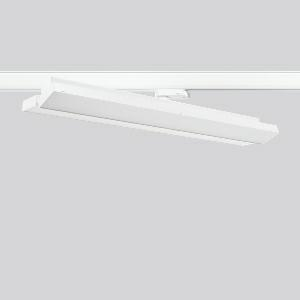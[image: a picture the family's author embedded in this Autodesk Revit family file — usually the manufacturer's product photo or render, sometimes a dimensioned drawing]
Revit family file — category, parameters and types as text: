
# Revit family: tx-move_742164_002_3_6d08
name_source: partatom
category: Lighting Fixtures
units: mm (PartAtom-declared; Revit-internal decimal feet)

## family parameters
Cut with Voids When Loaded = No
Host = Face
Light Source = No
Part Type = Normal
Room Calculation Point = No
Round Connector Dimension = Use Diameter
Shared = No

## types (1)
- MultiLumen 1 (1 x LED Modul 835, 2550 lm, 3500)
    Apparent Load = 41 VA
    CIE Flux Codes = 47 79 96 100 100
    Color Rendering = 80
    Color Temperature = 3500
    Default Elevation = 1800 mm
    Description = Series: TX-MOVE
Multifunctional surface-mounted spotlight for area lighting. Very flat design. Housing: sheet steel, powder-coated. Rotation range: 356°. Swivel range: 90°. Consistent alignment possible with visible tilt scale. High-efficiency LED units with flush-mounted opal diffuser made of non-yellowing PMMA. Symmetrical wide beam light emission. With multi adaptor for 3-circuit tracks 230 V. Suitable for Track on ceiling. MultiLumen: Luminous flux adjustable in 3 steps. Factory setting is the highest luminous flux. Environmentally friendly and resource-saving due to replaceable and recyclable components. 
Colour: traffic white, matt (RAL 9016)
Length: 570 mm
Width: 119 mm
Height: 92 mm
Lamp: LED
Socket: without socket
Colour temperature: 3500K
Colour rendering index (CRI): 80
System power: 41 W
Rated luminous flux: 5100 lm
Luminous efficiency: 124 lm/W
System power 2: 57 W
Rated luminous flux 2: 6950 lm
Luminous efficiency 2: 122 lm/W
System power 3: 73 W
Rated luminous flux 3: 8500 lm
Luminous efficiency 3: 116 lm/W
Control gear: Regulated power supply
Protection class: I
Type of protection: IP 20
    Height = 75 mm
    Lamp = 1 x LED Modul 835
    Lamp Light Flux = 2550 lm
    Lamp count = 1
    Length = 569 mm
    Lifetime = 50000 h
    Luminous efficacy = 124 lm/W
    Manufacturer = RZB
    ModVariant = No
    Model = 742164.002.3
    Mounting Place = Ceiling
    Mounting Type = Rail mounted
    Number of Poles = 1
    OnlyDefault = Yes
    Power Factor = 1
    Product Name = TX-MOVE
    Product group = Track mounted projectors
    ProductGroupID = 301
    Protection Class = Protection class I
    Protection Degree = IP 20
    RLX_Detail_Level = 1
    RLX_Emergency_Light_Flux = 0 lm
    RLX_Emergency_Type = 0
    RLX_Emergency_Type_DB = No
    RlxData = <blob elided: 29865 chars, md5=2e118d50>
    Socket = socket
    Standby Power = 0 W
    System Light Flux = 5100 lm
    System Power = 41 W
    Type Comments = MultiLumen 1
    Type Image = 742164.002.jpg
    URL = http://relux.com
    VarID = multilumen_1
    Voltage = 230 V
    Voltage Range = 220-240 V
    Weight = 0.00 kg
    Width = 119 mm

## geometry (parser evidence)
native form markers: Blend x4, Sweep x14
no freeform markers — native parametric forms only
